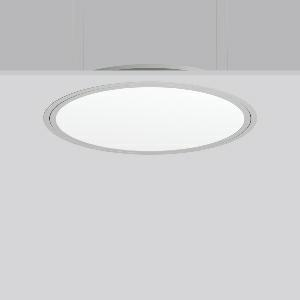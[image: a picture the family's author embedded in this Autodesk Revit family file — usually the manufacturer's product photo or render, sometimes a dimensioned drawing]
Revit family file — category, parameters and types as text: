
# Revit family: triona_round_e_312383_004_2_12_be40
name_source: partatom
category: Lighting Fixtures
units: mm (PartAtom-declared; Revit-internal decimal feet)

## family parameters
Cut with Voids When Loaded = No
Host = Face
Light Source = No
Part Type = Normal
Room Calculation Point = No
Round Connector Dimension = Use Diameter
Shared = No

## types (1)
- TuneableWhite 846 (1 x LED Modul 846, 3350 lm, 4600)
    Apparent Load = 40 VA
    CIE Flux Codes = 50 80 96 100 100
    Color Rendering = 80
    Color Temperature = 4600
    Default Elevation = 1800 mm
    Description = Series: TRIONA round
Decorative round LED recessed surface luminaire. Cover made of sheet steel, powder-coated. Frame made of aluminium, powder-coated. Recessed ring: aluminium extrusion profile, powder coated. Light emission through a diffuser: plastic, opal. Lightguide and diffuser made of non-yellowing plastic (PMMA). Lateral light emission (RZB SIDELITE technology) for above-average homogeneous light distribution. Tunable white versions, dynamically adjustable from 2700 K to 6500 K. Suitable for installation in cavity ceilings. Tool-free mounting system thanks to the rocker arm mechanism (patent pending). Electronic ballast included. Very easy installation thanks to Plug+Play connection. Ideal for use as part of the Human Centric Lighting concept in connection with RZB light management systems. 
Colour: silver, matt (approx. RAL 9006)
Diameter: 725 mm
Height: 2 mm
Cut-out diameter: 702 mm
Recess height: 100 mm
Luminaire: recess height: 89 mm
Lamp: LED
Socket: without socket
Colour temperature: 2700K - 6500K
Colour rendering index (CRI): 80
System power: 40 W
Rated luminous flux: 3350 lm
Luminous efficiency: 84 lm/W
System power 2: 42 W
Rated luminous flux 2: 3200 lm
Luminous efficiency 2: 76 lm/W
System power 3: 42 W
Rated luminous flux 3: 3250 lm
Luminous efficiency 3: 77 lm/W
Control gear: Converter, dimmable, DALI
Protection class: I
Type of protection: IP 40
    Height = 0 mm  [stored 0 ft]
    Lamp = 1 x LED Modul 846
    Lamp Light Flux = 3350 lm
    Lamp count = 1
    Length = 725 mm
    Lifetime = 50000 h
    Luminous efficacy = 84 lm/W
    Manufacturer = RZB
    ModVariant = No
    Model = 312383.004.2.12
    Mounting Place = Ceiling
    Mounting Type = Recessed
    Number of Poles = 1
    OnlyDefault = Yes
    Power Factor = 1
    Product Name = TRIONA round E
    Product group = Recessed modular luminaires
    ProductGroupID = 406
    Protection Class = Protection class I
    Protection Degree = IP 20
    RLX_Detail_Level = 1
    RLX_Emergency_Light_Flux = 0 lm
    RLX_Emergency_Type = 0
    RLX_Emergency_Type_DB = No
    RlxData = <blob elided: 35777 chars, md5=90d59089>
    Socket = socket
    Standby Power = 0 W
    System Light Flux = 3350 lm
    System Power = 40 W
    Type Comments = TuneableWhite 846
    Type Image = 312383.004.12.jpg
    URL = http://relux.com
    VarID = tuneablewhite_846
    Voltage = 230 V
    Voltage Range = 220-240 V
    Weight = 0.00 kg
    Width = 0 mm  [stored 0 ft]

note: [stored X ft] marks values corroborated as IEEE doubles in the binary element streams (Revit-internal decimal feet)

## geometry (parser evidence)
native form markers: Blend x4, Sweep x9
no freeform markers — native parametric forms only
